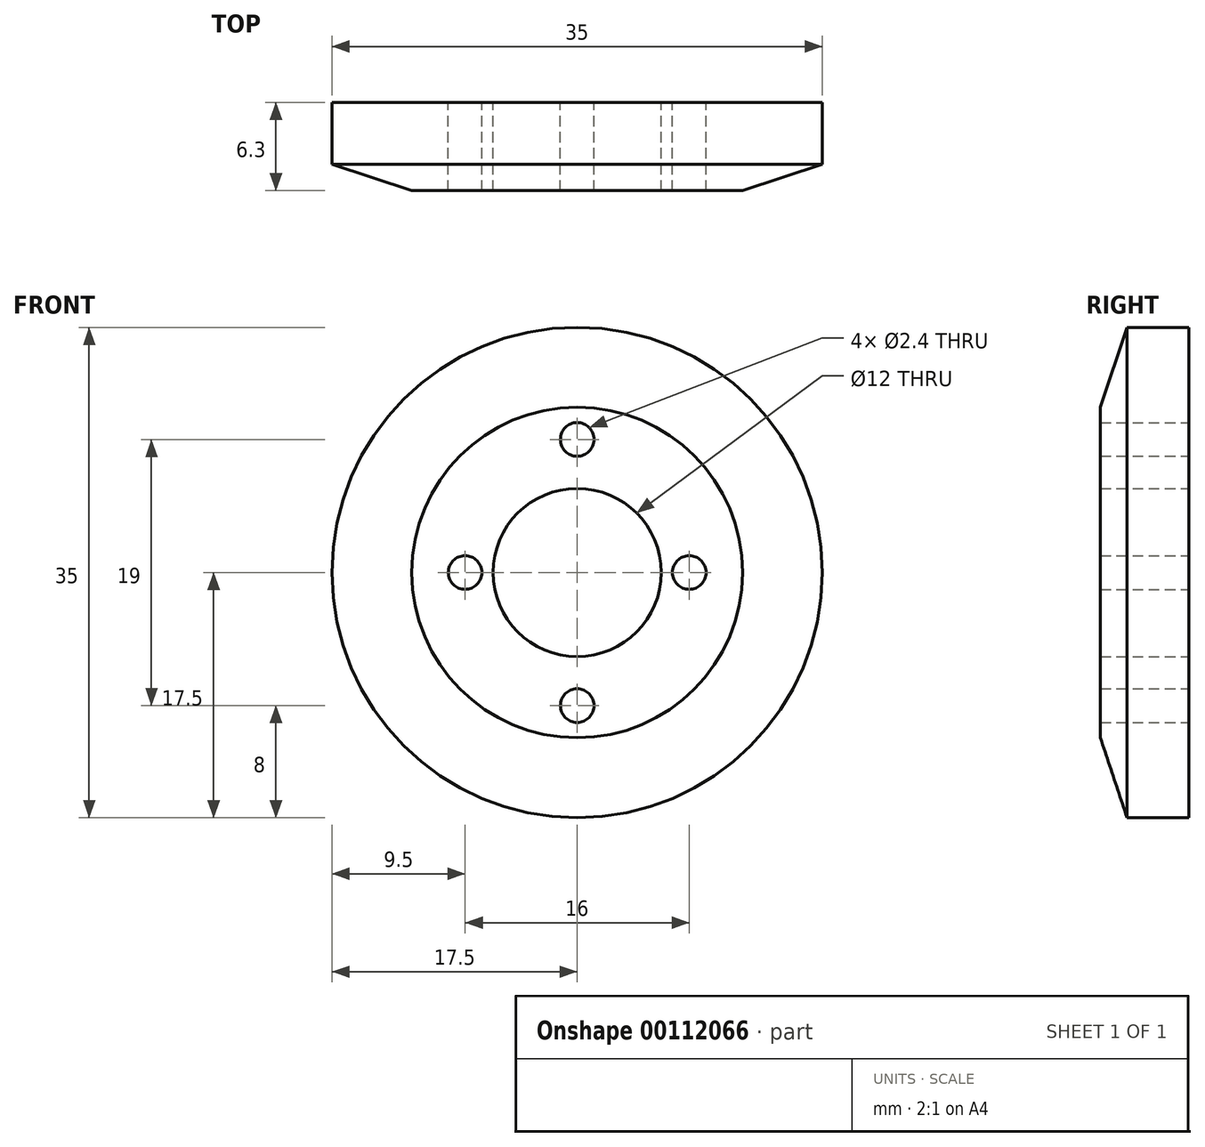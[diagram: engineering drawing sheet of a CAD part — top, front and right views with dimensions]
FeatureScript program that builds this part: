
annotation { "Feature Type Name" : "Feature", "Feature Type Description" : "" }
export const myFeature = defineFeature(function(context is Context, id is Id, definition is map)
    precondition{}
    {
        {
            var Q0;
            Q0=qCreatedBy(makeId("Front.planeOp"),FACE);
            var sketch = newSketch(context, id + "F0", { "sketchPlane" : qUnion([Q0])});
            skCircle(sketch, "E0", {"center": v(0, 0) * mm, "radius": 17.5 * mm});
            skCircle(sketch, "E1", {"center": v(0, 0) * mm, "radius": 6 * mm});
            skSolve(sketch);
        }
        {
            var Q0;
            Q0 = qSketchRegion(id + "F0", true);
            extrude(context, id + "F1", {"entities" : qUnion([Q0]), "depth" : 6.3 * mm});
        }
        {
            var Q0;
            Q0=makeQuery(id+"F1.opExtrude","CAP_EDGE",EDGE,{"disambiguationData":[OSD([sQuery(id+"F0.wireOp",EDGE,"E0")])],"isStart":false});
            chamfer(context, id + "F2", {"entities" : qUnion([Q0]), "chamferType" : ChamferType.TWO_OFFSETS, "width1" : 5.7 * mm, "oppositeDirection" : false, "width2" : 1.9 * mm, "tangentPropagation" : true});
        }
        {
            var Q0;
            Q0=makeQuery(id+"F1.opExtrude","CAP_FACE",FACE,{"disambiguationData":[OSD([sQuery(id+"F0.wireOp",EDGE,"E0"),sQuery(id+"F0.wireOp",EDGE,"E1")])],"isStart":false});
            var sketch = newSketch(context, id + "F3", { "sketchPlane" : qUnion([Q0])});
            skPoint(sketch, "E2", {"position": v(0, 9.5) * mm});
            skPoint(sketch, "E3", {"position": v(-8, 0) * mm});
            skPoint(sketch, "E4", {"position": v(0, -9.5) * mm});
            skPoint(sketch, "E5", {"position": v(8, 0) * mm});
            skSolve(sketch);
        }
        {
            var Q0;
            Q0=sQuery(id+"F3.wireOp",VERTEX,"E2");
            var Q1;
            Q1=sQuery(id+"F3.wireOp",VERTEX,"E3");
            var Q2;
            Q2=sQuery(id+"F3.wireOp",VERTEX,"E4");
            var Q3;
            Q3=sQuery(id+"F3.wireOp",VERTEX,"E5");
            var Q4;
            Q4=makeQuery(id+"F1.opExtrude","SWEPT_BODY",BODY,{"disambiguationData":[OSD([sQuery(id+"F0.wireOp",EDGE,"E0"),sQuery(id+"F0.wireOp",EDGE,"E1")])]});
            hole(context, id + "F4", {"style" : HoleStyle.SIMPLE, "endStyle" : HoleEndStyle.THROUGH, "standardTappedOrClearance" : lookupTablePath({ "standard" : "ISO", "engagement" : "75%", "pitch" : "0.6 mm", "size" : "M3", "type" : "Tapped" }), "standardBlindInLast" : lookupTablePath({ "standard" : "ISO", "engagement" : "75%", "pitch" : "0.6 mm", "size" : "M3", "type" : "Tapped" }), "holeDiameter" : 2.4 * mm, "locations" : qUnion([Q0, Q1, Q2, Q3]), "scope" : qUnion([Q4]), "isTappedThrough" : true, "showTappedDepth" : true});
        }
    });
